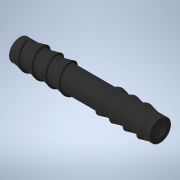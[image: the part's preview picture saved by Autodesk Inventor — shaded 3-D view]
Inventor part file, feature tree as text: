
AUTODESK INVENTOR PART (.ipt)
format: ipt  version: 2020 (Build 240168000, 168)  size: 238,592 bytes
history: native  units: mm
features: sketch x4, extrude x3, other x2, mirror x1, projected_geometry x1
ambient origin geometry x8: Origin, YZ Plane, XZ Plane, XY Plane, X Axis, Y Axis, Z Axis, Center Point
bodies: Volumenkörper1 (feature_tree), Solid2 (feature_tree), Solid3 (feature_tree)
feature tree (11):
  other  "Dribblerschnecke"
  extrude  "Extrusion1"  Depth=11.0mm
  other  "Spirale1"
  mirror  "Spiegeln1"
  extrude  "Extrusion5"  Depth=10.0mm
  extrude  "Extrusion6"  Depth=7.0mm
  sketch  "Skizze1"  dims[d0=6.0mm d1=11.0mm]
  sketch  "Skizze3"  dims[d2=36.0mm d3=0.0mm]
  projected_geometry  "Projizierte Kontur2"
  sketch  "Sketch7"  dims[d8=7.0mm d9=24.5mm d10=10.0mm d11=0.0mm d12=90.0deg d13=90.0deg d14=0.0mm d15=0.0mm d16=4.0mm]
  sketch  "Sketch8"  dims[d17=13.962634mm d18=1.0mm d19=0.1mm d32=10.0mm d33=0.0mm d34=7.0mm d35=100.0mm d36=0.0mm d37=82.0mm d38=0.0mm]
